# Revit family: Faucet-Wall_Mount-Lavatory-KOHLER-Purist-14419W_1
name_source: partatom
category: Plumbing Fixtures
revit_build: Autodesk Revit 2017 (Build: 20160225_1515(x64)
units: mm (PartAtom-declared; Revit-internal decimal feet)

## family parameters
Cut with Voids When Loaded = No
Host = Face
OmniClass Number = 23.31.11.00
OmniClass Title = Faucets
Part Type = Normal
Room Calculation Point = No
Round Connector Dimension = Use Diameter
Shared = No

## types (2) — shared parameters
ADA Compliant = No
Assembly Code = D2010
CW Connection = Yes
Cold Water Inlet = Cold Water Inlet
Date Modified = 06/18/2021
Default Elevation = 36"
Drain Included = No
Finish = Kohler-Metal-CP-Polished_Chrome
Flow Rate = 2 GPM
HW Connection = Yes
Height = 2"
Hot Water Inlet = Hot Water Inlet
Length = 5 5/16"
Manufacturer = KOHLER Co.
Master Format 2014 = 22 41 39
Master Format 2014 Name = Residential Faucets, Supplies, and Trim
Material = Premium Metal Construction
Pressure = 125.00 psi
Product Name = Purist
Product Page URL = https://www.kohler.co.uk
Spout Reach = 5 5/16"
URL = https://www.kohler.co.uk
Vent Connection = No
Waste Connection = No
Waste Water Outlet = Waste Water Outlet
WaterSense Certified = No

## per-type parameters (varying)
| type | Cross Handle | Description | Handle Clearance | Model | Type |
| Lever Handle, CP-Polished Chrome | No | Laminar 2-handle 3 hole wall-mount basin mixer, lever handle | 2 3/16" | 14419W-4-CP | 1 |
| Cross Handle, CP-Polished Chrome | Yes | Laminar 2-handle 3 hole wall-mount basin mixer, Cross handle | 1 1/2" | 14419W-3-CP | 2 |

## geometry (parser evidence)
native form markers: Sweep x5
no freeform markers — native parametric forms only
